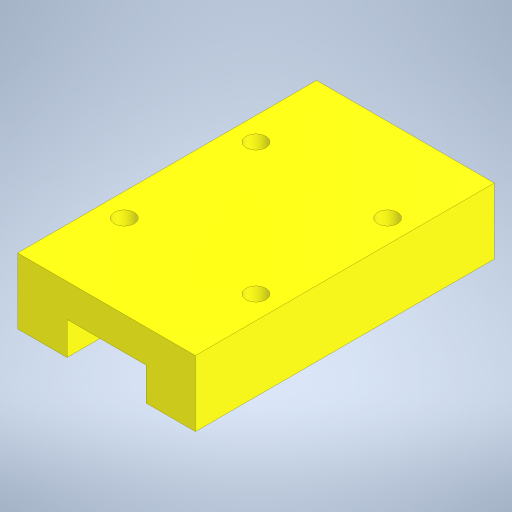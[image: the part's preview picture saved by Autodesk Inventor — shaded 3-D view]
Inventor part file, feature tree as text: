
AUTODESK INVENTOR PART (.ipt)
format: ipt  version: 2024 (Build 280153000, 153)  size: 236,544 bytes
history: native  units: mm
features: extrude x2, sketch x2
ambient origin geometry x8: Origin, YZ Plane, XZ Plane, XY Plane, X Axis, Y Axis, Z Axis, Center Point
bodies: Solid1 (feature_tree)
feature tree (4):
  extrude  "Extrusion1"  Depth=27.0mm
  extrude  "Extrusion2"  Depth=10.0mm
  sketch  "Sketch1"  dims[d0=12.0mm d1=27.0mm]
  sketch  "Sketch2"  dims[d2=7.5mm d3=10.0mm d4=5.0mm d5=45.4mm d6=0.0mm d7=3.0mm d8=3.0mm d9=3.0mm d10=3.0mm d11=20.0mm d12=20.0mm d13=20.0mm d14=3.5mm d15=12.7mm d16=12.7mm d17=12.7mm d18=12.7mm d19=0.0mm d20=0.0mm]
